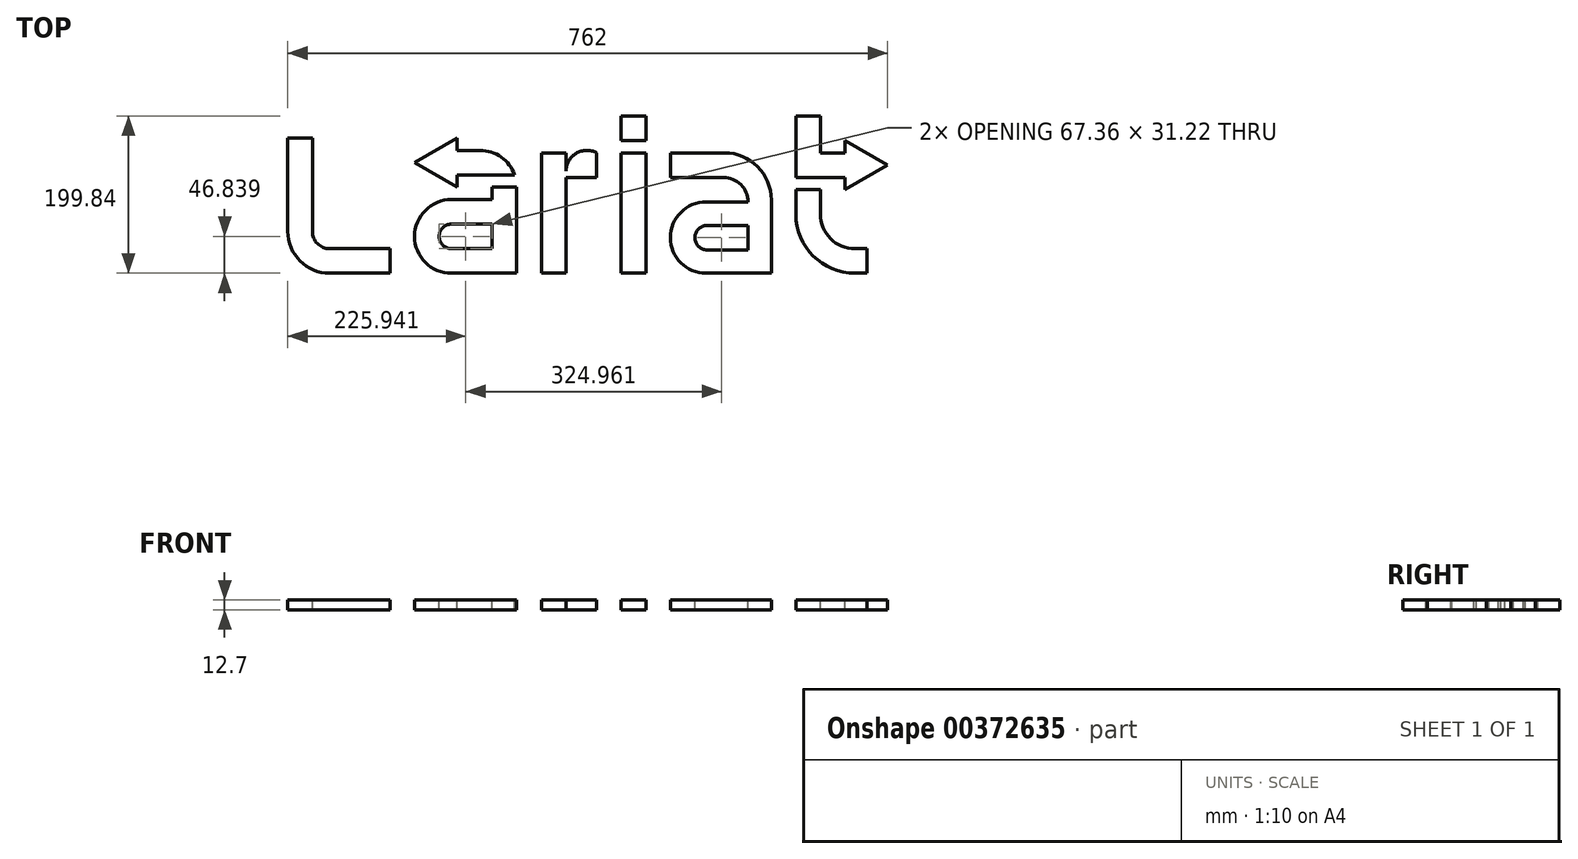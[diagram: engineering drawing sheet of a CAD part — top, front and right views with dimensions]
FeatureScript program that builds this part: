
annotation { "Feature Type Name" : "Feature", "Feature Type Description" : "" }
export const myFeature = defineFeature(function(context is Context, id is Id, definition is map)
    precondition{}
    {
        {
            var Q0;
            Q0=qCreatedBy(makeId("Top.planeOp"),FACE);
            var sketch = newSketch(context, id + "F0", { "sketchPlane" : qUnion([Q0])});
            skLineSegment(sketch, "E0", {"start": v(-165.88, 71.82) * mm, "end": v(-219.96, 40.6) * mm});
            skLineSegment(sketch, "E1", {"start": v(-219.96, 40.6) * mm, "end": v(-165.88, 9.37) * mm});
            skLineSegment(sketch, "E2", {"start": v(-165.88, 9.37) * mm, "end": v(-165.88, 24.98) * mm});
            skLineSegment(sketch, "E3", {"start": v(-165.88, 24.98) * mm, "end": v(-92.83, 24.98) * mm});
            skLineSegment(sketch, "E4", {"start": v(-136.99, 56.2) * mm, "end": v(-165.88, 56.2) * mm});
            skLineSegment(sketch, "E5", {"start": v(-165.88, 56.2) * mm, "end": v(-165.88, 71.82) * mm});
            skLineSegment(sketch, "E6", {"start": v(-381, 71.82) * mm, "end": v(-381, -46.61) * mm});
            skLineSegment(sketch, "E7", {"start": v(-327.7, -99.92) * mm, "end": v(-251.19, -99.92) * mm});
            skLineSegment(sketch, "E8", {"start": v(-251.19, -99.92) * mm, "end": v(-251.19, -68.7) * mm});
            skLineSegment(sketch, "E9", {"start": v(-251.19, -68.7) * mm, "end": v(-327.7, -68.7) * mm});
            skLineSegment(sketch, "E10", {"start": v(-349.78, -46.61) * mm, "end": v(-349.78, 71.82) * mm});
            skLineSegment(sketch, "E11", {"start": v(-349.78, 71.82) * mm, "end": v(-381, 71.82) * mm});
            skLineSegment(sketch, "E12", {"start": v(-27.7, 29.66) * mm, "end": v(-27.7, 53.08) * mm});
            skLineSegment(sketch, "E13", {"start": v(-27.7, 53.08) * mm, "end": v(-58.93, 53.08) * mm});
            skLineSegment(sketch, "E14", {"start": v(-58.93, 53.08) * mm, "end": v(-58.93, -99.92) * mm});
            skLineSegment(sketch, "E15", {"start": v(-58.93, -99.92) * mm, "end": v(-27.7, -99.92) * mm});
            skLineSegment(sketch, "E16", {"start": v(-27.7, -99.92) * mm, "end": v(-27.7, 21.86) * mm});
            skLineSegment(sketch, "E17", {"start": v(-27.7, 21.86) * mm, "end": v(3.52, 21.86) * mm});
            skLineSegment(sketch, "E18", {"start": v(3.52, 21.86) * mm, "end": v(3.52, 53.08) * mm, "construction": true});
            skLineSegment(sketch, "E19", {"start": v(-121.38, 9.37) * mm, "end": v(-121.38, -6.24) * mm});
            skLineSegment(sketch, "E20", {"start": v(-121.38, -6.24) * mm, "end": v(-173.13, -6.24) * mm});
            skLineSegment(sketch, "E21", {"start": v(-173.13, -99.92) * mm, "end": v(-90.15, -99.92) * mm});
            skLineSegment(sketch, "E22", {"start": v(-90.15, -99.92) * mm, "end": v(-90.15, 9.37) * mm});
            skLineSegment(sketch, "E23", {"start": v(-90.15, 9.37) * mm, "end": v(-121.38, 9.37) * mm});
            skLineSegment(sketch, "E24", {"start": v(-173.13, -37.47) * mm, "end": v(-121.38, -37.47) * mm});
            skLineSegment(sketch, "E25", {"start": v(-121.38, -37.47) * mm, "end": v(-121.38, -68.7) * mm});
            skLineSegment(sketch, "E26", {"start": v(-121.38, -68.7) * mm, "end": v(-173.13, -68.7) * mm});
            skPoint(sketch, "E27.middle", {"position": v(0, 0) * mm});
            skArc(sketch, "E28", {"start": v(-349.78, -46.61) * mm, "mid": v(-343.3, -62.23) * mm, "end": v(-327.7, -68.7) * mm});
            skArc(sketch, "E29", {"start": v(-381, -46.61) * mm, "mid": v(-365.39, -84.3) * mm, "end": v(-327.7, -99.92) * mm});
            skArc(sketch, "E30", {"start": v(-173.13, -37.47) * mm, "mid": v(-188.74, -53.08) * mm, "end": v(-173.13, -68.7) * mm});
            skArc(sketch, "E31", {"start": v(-173.13, -6.24) * mm, "mid": v(-219.96, -53.08) * mm, "end": v(-173.13, -99.92) * mm});
            skLineSegment(sketch, "E32", {"start": v(-121.38, -37.47) * mm, "end": v(-121.38, -21.86) * mm, "construction": true});
            skLineSegment(sketch, "E33", {"start": v(-121.38, -68.7) * mm, "end": v(-121.38, -99.92) * mm, "construction": true});
            skLineSegment(sketch, "E34", {"start": v(-188.74, -53.08) * mm, "end": v(-219.96, -53.08) * mm, "construction": true});
            skPoint(sketch, "E35", {"position": v(-121.38, -21.86) * mm});
            skLineSegment(sketch, "E36", {"start": v(-121.38, -21.86) * mm, "end": v(-121.38, -6.24) * mm, "construction": true});
            skLineSegment(sketch, "E37", {"start": v(-105.77, 9.37) * mm, "end": v(-105.77, 24.98) * mm, "construction": true});
            skLineSegment(sketch, "E38", {"start": v(-92.83, 40.6) * mm, "end": v(-219.96, 40.6) * mm, "construction": true});
            skLineSegment(sketch, "E39", {"start": v(-121.38, -21.86) * mm, "end": v(-90.15, -21.86) * mm, "construction": true});
            skLineSegment(sketch, "E40", {"start": v(-219.96, 40.6) * mm, "end": v(-219.96, -53.08) * mm, "construction": true});
            skLineSegment(sketch, "E41", {"start": v(-92.83, 56.2) * mm, "end": v(-92.83, 24.98) * mm, "construction": true});
            skArc(sketch, "E42", {"start": v(-92.83, 24.98) * mm, "mid": v(-109.95, 47.6) * mm, "end": v(-136.99, 56.2) * mm});
            skLineSegment(sketch, "E43", {"start": v(-251.19, 71.82) * mm, "end": v(-381, 71.82) * mm, "construction": true});
            skLineSegment(sketch, "E44", {"start": v(-219.96, -53.08) * mm, "end": v(-219.96, -99.92) * mm, "construction": true});
            skLineSegment(sketch, "E45", {"start": v(-219.96, -99.92) * mm, "end": v(-90.15, -99.92) * mm, "construction": true});
            skLineSegment(sketch, "E46", {"start": v(-165.88, 71.82) * mm, "end": v(-165.88, -99.92) * mm, "construction": true});
            skLineSegment(sketch, "E47", {"start": v(-251.19, 71.82) * mm, "end": v(-251.19, -99.92) * mm, "construction": true});
            skLineSegment(sketch, "E48", {"start": v(-349.78, -46.61) * mm, "end": v(-327.7, -68.7) * mm, "construction": true});
            skLineSegment(sketch, "E49", {"start": v(-381, -46.61) * mm, "end": v(-327.7, -99.92) * mm, "construction": true});
            skLineSegment(sketch, "E50", {"start": v(-165.88, -14.05) * mm, "end": v(-251.19, -14.05) * mm, "construction": true});
            skLineSegment(sketch, "E51", {"start": v(-219.96, -53.08) * mm, "end": v(-251.19, -53.08) * mm, "construction": true});
            skLineSegment(sketch, "E52", {"start": v(-27.7, 21.86) * mm, "end": v(-43.32, 21.86) * mm, "construction": true});
            skPoint(sketch, "E53", {"position": v(-43.32, 21.86) * mm});
            skPoint(sketch, "E54.orphan", {"position": v(-58.93, 21.86) * mm});
            skLineSegment(sketch, "E55", {"start": v(-43.32, 21.86) * mm, "end": v(-51.12, 21.86) * mm, "construction": true});
            skPoint(sketch, "E56", {"position": v(-51.12, 21.86) * mm});
            skLineSegment(sketch, "E57", {"start": v(-51.12, 21.86) * mm, "end": v(-58.93, 21.86) * mm, "construction": true});
            skLineSegment(sketch, "E58", {"start": v(-27.7, 21.86) * mm, "end": v(-27.7, 29.66) * mm, "construction": true});
            skLineSegment(sketch, "E59", {"start": v(-27.7, 53.08) * mm, "end": v(3.52, 53.08) * mm, "construction": true});
            skLineSegment(sketch, "E60", {"start": v(3.52, 21.86) * mm, "end": v(11.32, 21.86) * mm});
            skLineSegment(sketch, "E61", {"start": v(3.52, 53.08) * mm, "end": v(11.32, 53.08) * mm, "construction": true});
            skLineSegment(sketch, "E62", {"start": v(11.32, 53.08) * mm, "end": v(11.32, 21.86) * mm});
            skArc(sketch, "E63", {"start": v(11.32, 53.08) * mm, "mid": v(-14.82, 52.42) * mm, "end": v(-27.7, 29.66) * mm});
            skLineSegment(sketch, "E64", {"start": v(-136.99, 56.2) * mm, "end": v(-1.17, 56.2) * mm, "construction": true});
            skLineSegment(sketch, "E65", {"start": v(-90.15, -99.92) * mm, "end": v(-58.93, -99.92) * mm, "construction": true});
            skLineSegment(sketch, "E66.bottom", {"start": v(42.55, 53.08) * mm, "end": v(73.77, 53.08) * mm});
            skLineSegment(sketch, "E66.top", {"start": v(42.55, -99.92) * mm, "end": v(73.77, -99.92) * mm});
            skLineSegment(sketch, "E66.left", {"start": v(42.55, 53.08) * mm, "end": v(42.55, -99.92) * mm});
            skLineSegment(sketch, "E66.right", {"start": v(73.77, 53.08) * mm, "end": v(73.77, -99.92) * mm});
            skLineSegment(sketch, "E67.bottom", {"start": v(42.55, 99.92) * mm, "end": v(73.77, 99.92) * mm});
            skLineSegment(sketch, "E67.top", {"start": v(42.55, 68.7) * mm, "end": v(73.77, 68.7) * mm});
            skLineSegment(sketch, "E67.left", {"start": v(42.55, 99.92) * mm, "end": v(42.55, 68.7) * mm});
            skLineSegment(sketch, "E67.right", {"start": v(73.77, 99.92) * mm, "end": v(73.77, 68.7) * mm});
            skLineSegment(sketch, "E68", {"start": v(58.16, 68.7) * mm, "end": v(58.16, 53.08) * mm, "construction": true});
            skLineSegment(sketch, "E69", {"start": v(42.55, 68.7) * mm, "end": v(42.55, 53.08) * mm, "construction": true});
            skLineSegment(sketch, "E70", {"start": v(73.77, 68.7) * mm, "end": v(73.77, 53.08) * mm, "construction": true});
            skLineSegment(sketch, "E71", {"start": v(105, 21.86) * mm, "end": v(172.36, 21.86) * mm});
            skLineSegment(sketch, "E72", {"start": v(173.49, 53.08) * mm, "end": v(105, 53.08) * mm});
            skLineSegment(sketch, "E73", {"start": v(203.58, -9.37) * mm, "end": v(150.27, -9.37) * mm});
            skLineSegment(sketch, "E74", {"start": v(150.27, -99.92) * mm, "end": v(233.25, -99.92) * mm});
            skLineSegment(sketch, "E75", {"start": v(233.25, -99.92) * mm, "end": v(233.25, -6.68) * mm});
            skLineSegment(sketch, "E76", {"start": v(151.83, -39.03) * mm, "end": v(203.58, -39.03) * mm});
            skLineSegment(sketch, "E77", {"start": v(203.58, -39.03) * mm, "end": v(203.58, -70.25) * mm});
            skLineSegment(sketch, "E78", {"start": v(203.58, -70.25) * mm, "end": v(151.83, -70.25) * mm});
            skArc(sketch, "E79", {"start": v(151.83, -39.03) * mm, "mid": v(136.22, -54.64) * mm, "end": v(151.83, -70.25) * mm});
            skArc(sketch, "E80", {"start": v(150.27, -9.37) * mm, "mid": v(105, -54.64) * mm, "end": v(150.27, -99.92) * mm});
            skLineSegment(sketch, "E81", {"start": v(203.58, -39.03) * mm, "end": v(203.58, -24.2) * mm, "construction": true});
            skLineSegment(sketch, "E82", {"start": v(203.58, -70.25) * mm, "end": v(203.58, -99.92) * mm, "construction": true});
            skLineSegment(sketch, "E83", {"start": v(136.22, -54.64) * mm, "end": v(105, -54.64) * mm, "construction": true});
            skPoint(sketch, "E84", {"position": v(203.58, -24.2) * mm});
            skLineSegment(sketch, "E85", {"start": v(203.58, -24.2) * mm, "end": v(203.58, -9.37) * mm, "construction": true});
            skLineSegment(sketch, "E86", {"start": v(213.76, 37.47) * mm, "end": v(105, 37.47) * mm, "construction": true});
            skLineSegment(sketch, "E87", {"start": v(203.58, -24.2) * mm, "end": v(233.25, -24.2) * mm, "construction": true});
            skLineSegment(sketch, "E88", {"start": v(105, 37.47) * mm, "end": v(105, -54.64) * mm, "construction": true});
            skArc(sketch, "E89", {"start": v(233.25, -6.68) * mm, "mid": v(215.74, 35.58) * mm, "end": v(173.49, 53.08) * mm});
            skLineSegment(sketch, "E90", {"start": v(105, -54.64) * mm, "end": v(105, -99.92) * mm, "construction": true});
            skLineSegment(sketch, "E91", {"start": v(105, -99.92) * mm, "end": v(233.25, -99.92) * mm, "construction": true});
            skArc(sketch, "E92", {"start": v(203.58, -9.37) * mm, "mid": v(194.44, 12.71) * mm, "end": v(172.36, 21.86) * mm});
            skLineSegment(sketch, "E93", {"start": v(173.49, 53.08) * mm, "end": v(233.25, -6.68) * mm, "construction": true});
            skLineSegment(sketch, "E94", {"start": v(172.36, 21.86) * mm, "end": v(203.58, -9.37) * mm, "construction": true});
            skLineSegment(sketch, "E95", {"start": v(172.36, 53.08) * mm, "end": v(172.36, 37.47) * mm, "construction": true});
            skLineSegment(sketch, "E96", {"start": v(172.36, 37.47) * mm, "end": v(172.36, 21.86) * mm, "construction": true});
            skLineSegment(sketch, "E97", {"start": v(105, 21.86) * mm, "end": v(105, 53.08) * mm});
            skLineSegment(sketch, "E98", {"start": v(150.27, -9.37) * mm, "end": v(150.27, 21.86) * mm, "construction": true});
            skLineSegment(sketch, "E99", {"start": v(172.36, 53.08) * mm, "end": v(172.36, -99.92) * mm, "construction": true});
            skLineSegment(sketch, "E100", {"start": v(11.32, 37.47) * mm, "end": v(42.55, 37.47) * mm, "construction": true});
            skLineSegment(sketch, "E101", {"start": v(105, 37.47) * mm, "end": v(73.77, 37.47) * mm, "construction": true});
            skLineSegment(sketch, "E102.bottom", {"start": v(264.47, 99.92) * mm, "end": v(295.7, 99.92) * mm});
            skLineSegment(sketch, "E102.top", {"start": v(264.47, 21.86) * mm, "end": v(295.7, 21.86) * mm});
            skLineSegment(sketch, "E102.left", {"start": v(264.47, 99.92) * mm, "end": v(264.47, 21.86) * mm});
            skLineSegment(sketch, "E102.right", {"start": v(295.7, 99.92) * mm, "end": v(295.7, 53.08) * mm});
            skLineSegment(sketch, "E103", {"start": v(105, 21.86) * mm, "end": v(11.32, 21.86) * mm, "construction": true});
            skLineSegment(sketch, "E104", {"start": v(105, -99.92) * mm, "end": v(-27.7, -99.92) * mm, "construction": true});
            skLineSegment(sketch, "E105", {"start": v(58.16, 99.92) * mm, "end": v(58.16, 21.86) * mm, "construction": true});
            skLineSegment(sketch, "E106", {"start": v(280.08, 99.92) * mm, "end": v(280.08, -99.92) * mm, "construction": true});
            skPoint(sketch, "E106.endSnap0", {"position": v(280.08, 21.86) * mm});
            skLineSegment(sketch, "E107", {"start": v(233.25, -99.92) * mm, "end": v(280.08, -99.92) * mm, "construction": true});
            skLineSegment(sketch, "E108", {"start": v(295.7, 53.08) * mm, "end": v(326.92, 53.08) * mm});
            skLineSegment(sketch, "E109", {"start": v(326.92, 21.86) * mm, "end": v(295.7, 21.86) * mm});
            skLineSegment(sketch, "E110", {"start": v(326.92, 53.08) * mm, "end": v(326.92, 68.7) * mm});
            skLineSegment(sketch, "E111", {"start": v(326.92, 21.86) * mm, "end": v(326.92, 6.24) * mm});
            skLineSegment(sketch, "E112", {"start": v(326.92, 68.7) * mm, "end": v(381, 37.47) * mm});
            skLineSegment(sketch, "E113", {"start": v(381, 37.47) * mm, "end": v(326.92, 6.24) * mm});
            skLineSegment(sketch, "E114", {"start": v(311.3, 53.08) * mm, "end": v(311.3, 21.86) * mm, "construction": true});
            skLineSegment(sketch, "E115", {"start": v(295.7, 21.86) * mm, "end": v(295.7, 6.24) * mm, "construction": true});
            skLineSegment(sketch, "E116", {"start": v(264.47, 21.86) * mm, "end": v(264.47, 6.24) * mm, "construction": true});
            skLineSegment(sketch, "E117", {"start": v(264.47, 6.24) * mm, "end": v(295.7, 6.24) * mm});
            skLineSegment(sketch, "E118", {"start": v(264.47, 6.24) * mm, "end": v(264.47, -24.98) * mm});
            skLineSegment(sketch, "E119", {"start": v(295.7, 6.24) * mm, "end": v(295.7, -24.98) * mm});
            skLineSegment(sketch, "E120", {"start": v(355.02, -68.7) * mm, "end": v(355.02, -99.92) * mm});
            skLineSegment(sketch, "E121", {"start": v(355.02, -99.92) * mm, "end": v(339.4, -99.92) * mm});
            skLineSegment(sketch, "E122", {"start": v(355.02, -68.7) * mm, "end": v(339.4, -68.7) * mm});
            skArc(sketch, "E123.trimOffspring", {"start": v(295.7, -24.98) * mm, "mid": v(308.5, -55.89) * mm, "end": v(339.4, -68.7) * mm});
            skArc(sketch, "E124.trimOffspring", {"start": v(264.47, -24.98) * mm, "mid": v(286.42, -77.97) * mm, "end": v(339.4, -99.92) * mm});
            skLineSegment(sketch, "E125", {"start": v(295.7, -24.98) * mm, "end": v(339.4, -68.7) * mm, "construction": true});
            skLineSegment(sketch, "E126", {"start": v(264.47, -24.98) * mm, "end": v(339.4, -99.92) * mm, "construction": true});
            skLineSegment(sketch, "E127", {"start": v(339.4, -68.7) * mm, "end": v(339.4, -99.92) * mm, "construction": true});
            skLineSegment(sketch, "E128", {"start": v(295.7, -24.98) * mm, "end": v(264.47, -24.98) * mm, "construction": true});
            skLineSegment(sketch, "E129", {"start": v(264.47, -9.37) * mm, "end": v(233.25, -9.37) * mm, "construction": true});
            skLineSegment(sketch, "E130", {"start": v(-90.15, -6.24) * mm, "end": v(-219.96, -6.24) * mm, "construction": true});
            skLineSegment(sketch, "E131.bottom", {"start": v(-381, 99.92) * mm, "end": v(381, 99.92) * mm, "construction": true});
            skLineSegment(sketch, "E131.top", {"start": v(-381, -99.92) * mm, "end": v(381, -99.92) * mm, "construction": true});
            skLineSegment(sketch, "E131.left", {"start": v(-381, 99.92) * mm, "end": v(-381, -99.92) * mm, "construction": true});
            skLineSegment(sketch, "E131.right", {"start": v(381, 99.92) * mm, "end": v(381, -99.92) * mm, "construction": true});
            skLineSegment(sketch, "E132", {"start": v(-327.7, -68.7) * mm, "end": v(-327.7, -99.92) * mm, "construction": true});
            skLineSegment(sketch, "E133", {"start": v(-349.78, -46.61) * mm, "end": v(-381, -46.61) * mm, "construction": true});
            skPoint(sketch, "E134.end.orphan", {"position": v(-343.3, -62.23) * mm});
            skPoint(sketch, "E135.end.orphan", {"position": v(-365.39, -84.3) * mm});
            skLineSegment(sketch, "E136", {"start": v(-343.3, -62.23) * mm, "end": v(-365.39, -84.3) * mm, "construction": true});
            skPoint(sketch, "E137", {"position": v(301.94, -62.45) * mm});
            skLineSegment(sketch, "E138", {"start": v(308.5, -55.89) * mm, "end": v(286.42, -77.97) * mm, "construction": true});
            skLineSegment(sketch, "E139", {"start": v(216.52, 34.8) * mm, "end": v(194.44, 12.71) * mm, "construction": true});
            skPoint(sketch, "E140", {"position": v(194.44, 12.71) * mm});
            skLineSegment(sketch, "E141", {"start": v(0, 99.92) * mm, "end": v(0, -99.92) * mm, "construction": true});
            skLineSegment(sketch, "E142.bottom", {"start": v(-431.8, 150.72) * mm, "end": v(431.8, 150.72) * mm, "construction": true});
            skLineSegment(sketch, "E142.top", {"start": v(-431.8, -150.72) * mm, "end": v(431.8, -150.72) * mm, "construction": true});
            skLineSegment(sketch, "E142.left", {"start": v(-431.8, 150.72) * mm, "end": v(-431.8, -150.72) * mm, "construction": true});
            skLineSegment(sketch, "E142.right", {"start": v(431.8, 150.72) * mm, "end": v(431.8, -150.72) * mm, "construction": true});
            skSolve(sketch);
        }
        {
            var Q0;
            Q0=makeQuery(id+"F0.imprint","IMPRINT",FACE,{"disambiguationData":[TD([[makeQuery(id+"F0.imprint","IMPRINT",EDGE,{"derivedFrom":sQuery(id+"F0.wireOp",EDGE,"E12")}),1.0]])]});
            var Q1;
            Q1=makeQuery(id+"F0.imprint","IMPRINT",FACE,{"disambiguationData":[TD([[makeQuery(id+"F0.imprint","IMPRINT",EDGE,{"derivedFrom":sQuery(id+"F0.wireOp",EDGE,"E19")}),1.0]])]});
            var Q2;
            Q2=makeQuery(id+"F0.imprint","IMPRINT",FACE,{"disambiguationData":[TD([[makeQuery(id+"F0.imprint","IMPRINT",EDGE,{"derivedFrom":sQuery(id+"F0.wireOp",EDGE,"E0")}),1.0]])]});
            var Q3;
            Q3=makeQuery(id+"F0.imprint","IMPRINT",FACE,{"disambiguationData":[TD([[makeQuery(id+"F0.imprint","IMPRINT",EDGE,{"derivedFrom":sQuery(id+"F0.wireOp",EDGE,"E6")}),1.0]])]});
            var Q4;
            Q4=makeQuery(id+"F0.imprint","IMPRINT",FACE,{"disambiguationData":[TD([[makeQuery(id+"F0.imprint","IMPRINT",EDGE,{"derivedFrom":sQuery(id+"F0.wireOp",EDGE,"E66.bottom")}),-1.0]])]});
            var Q5;
            Q5=makeQuery(id+"F0.imprint","IMPRINT",FACE,{"disambiguationData":[TD([[makeQuery(id+"F0.imprint","IMPRINT",EDGE,{"derivedFrom":sQuery(id+"F0.wireOp",EDGE,"E67.bottom")}),-1.0]])]});
            var Q6;
            Q6=makeQuery(id+"F0.imprint","IMPRINT",FACE,{"disambiguationData":[TD([[makeQuery(id+"F0.imprint","IMPRINT",EDGE,{"derivedFrom":sQuery(id+"F0.wireOp",EDGE,"E71")}),1.0]])]});
            var Q7;
            Q7=makeQuery(id+"F0.imprint","IMPRINT",FACE,{"disambiguationData":[TD([[makeQuery(id+"F0.imprint","IMPRINT",EDGE,{"derivedFrom":sQuery(id+"F0.wireOp",EDGE,"E117")}),-1.0]])]});
            var Q8;
            Q8=makeQuery(id+"F0.imprint","IMPRINT",FACE,{"disambiguationData":[TD([[makeQuery(id+"F0.imprint","IMPRINT",EDGE,{"derivedFrom":sQuery(id+"F0.wireOp",EDGE,"E102.bottom")}),-1.0]])]});
            extrude(context, id + "F1", {"entities" : qUnion([Q0, Q1, Q2, Q3, Q4, Q5, Q6, Q7, Q8]), "oppositeDirection" : true, "depth" : 12.7 * mm, "offsetDistance" : 25.4 * mm});
        }
    });
